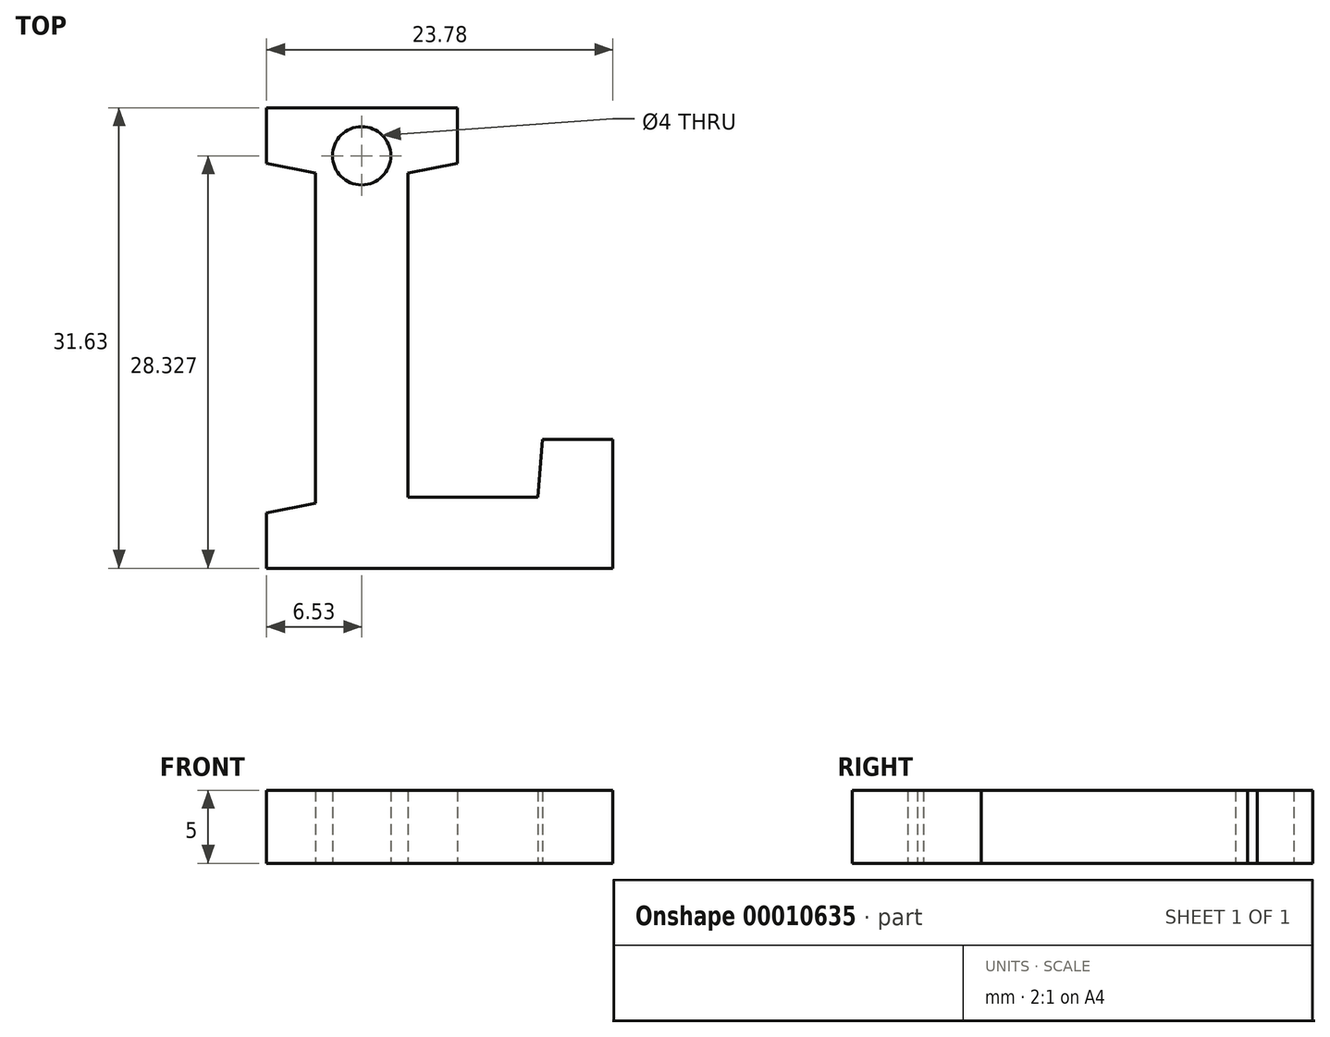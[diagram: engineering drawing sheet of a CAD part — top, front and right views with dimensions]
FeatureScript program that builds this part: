
annotation { "Feature Type Name" : "Feature", "Feature Type Description" : "" }
export const myFeature = defineFeature(function(context is Context, id is Id, definition is map)
    precondition{}
    {
        {
            var Q0;
            Q0=qCreatedBy(makeId("Top.planeOp"),FACE);
            var sketch = newSketch(context, id + "F0", { "sketchPlane" : qUnion([Q0])});
            skText(sketch, "E0", { "text": "L", "fontName": "RobotoSlab-Bold.ttf"});
            const initialGuessF0  = {"E0": [0, -0.03203, 1, 0, 0.03203]};
            skSetInitialGuess(sketch, initialGuessF0);
            skSolve(sketch);
        }
        {
            var Q0;
            Q0 = qSketchRegion(id + "F0", true);
            extrude(context, id + "F1", {"entities" : qUnion([Q0]), "depth" : 5 * mm});
        }
        {
            var Q0;
            Q0=qCreatedBy(makeId("Top.planeOp"),FACE);
            var sketch = newSketch(context, id + "F2", { "sketchPlane" : qUnion([Q0])});
            skCircle(sketch, "E1", {"center": v(7.75, -3.7) * mm, "radius": 2 * mm});
            skSolve(sketch);
        }
        {
            var Q0;
            Q0 = qSketchRegion(id + "F2", true);
            extrude(context, id + "F3", {"entities" : qUnion([Q0]), "operationType" : NewBodyOperationType.REMOVE, "endBound" : BoundingType.THROUGH_ALL, "depth" : 25 * mm});
        }
    });
